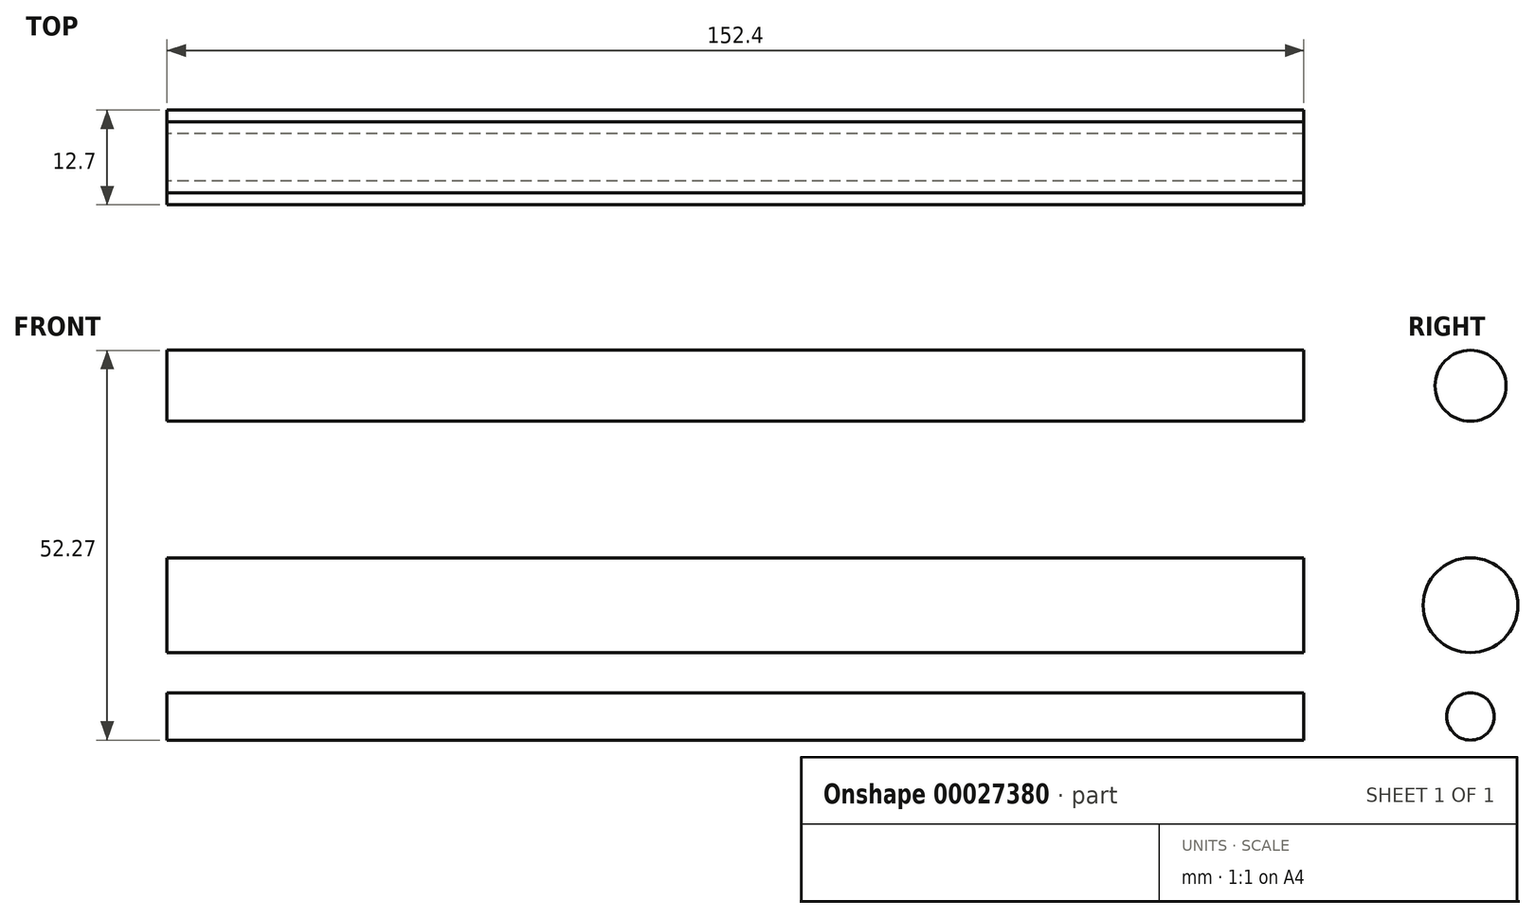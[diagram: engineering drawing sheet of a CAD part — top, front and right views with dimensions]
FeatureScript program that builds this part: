
annotation { "Feature Type Name" : "Feature", "Feature Type Description" : "" }
export const myFeature = defineFeature(function(context is Context, id is Id, definition is map)
    precondition{}
    {
        {
            var Q0;
            Q0=qCreatedBy(makeId("Right.planeOp"),FACE);
            var sketch = newSketch(context, id + "F0", { "sketchPlane" : qUnion([Q0])});
            skCircle(sketch, "E0", {"center": v(0, 0) * mm, "radius": 6.35 * mm});
            skCircle(sketch, "E1", {"center": v(0, 29.43) * mm, "radius": 4.76 * mm});
            skSolve(sketch);
        }
        {
            var Q0;
            Q0=makeQuery(id+"F0.imprint","IMPRINT",FACE,{"disambiguationData":[TD([[makeQuery(id+"F0.imprint","IMPRINT",EDGE,{"derivedFrom":sQuery(id+"F0.wireOp",EDGE,"E0")}),1.0]])]});
            extrude(context, id + "F1", {"entities" : qUnion([Q0]), "depth" : 152.4 * mm});
        }
        {
            var Q0;
            Q0=qCreatedBy(makeId("Right.planeOp"),FACE);
            var sketch = newSketch(context, id + "F2", { "sketchPlane" : qUnion([Q0])});
            skCircle(sketch, "E2", {"center": v(0, -14.9) * mm, "radius": 3.18 * mm});
            skSolve(sketch);
        }
        {
            var Q0;
            Q0=makeQuery(id+"F2.imprint","IMPRINT",FACE,{"disambiguationData":[TD([[makeQuery(id+"F2.imprint","IMPRINT",EDGE,{"derivedFrom":sQuery(id+"F2.wireOp",EDGE,"E2")}),1.0]])]});
            extrude(context, id + "F3", {"entities" : qUnion([Q0]), "depth" : 152.4 * mm});
        }
        {
            var Q0;
            Q0=makeQuery(id+"F0.imprint","IMPRINT",FACE,{"disambiguationData":[TD([[makeQuery(id+"F0.imprint","IMPRINT",EDGE,{"derivedFrom":sQuery(id+"F0.wireOp",EDGE,"E1")}),1.0]])]});
            extrude(context, id + "F4", {"entities" : qUnion([Q0]), "depth" : 152.4 * mm});
        }
    });
